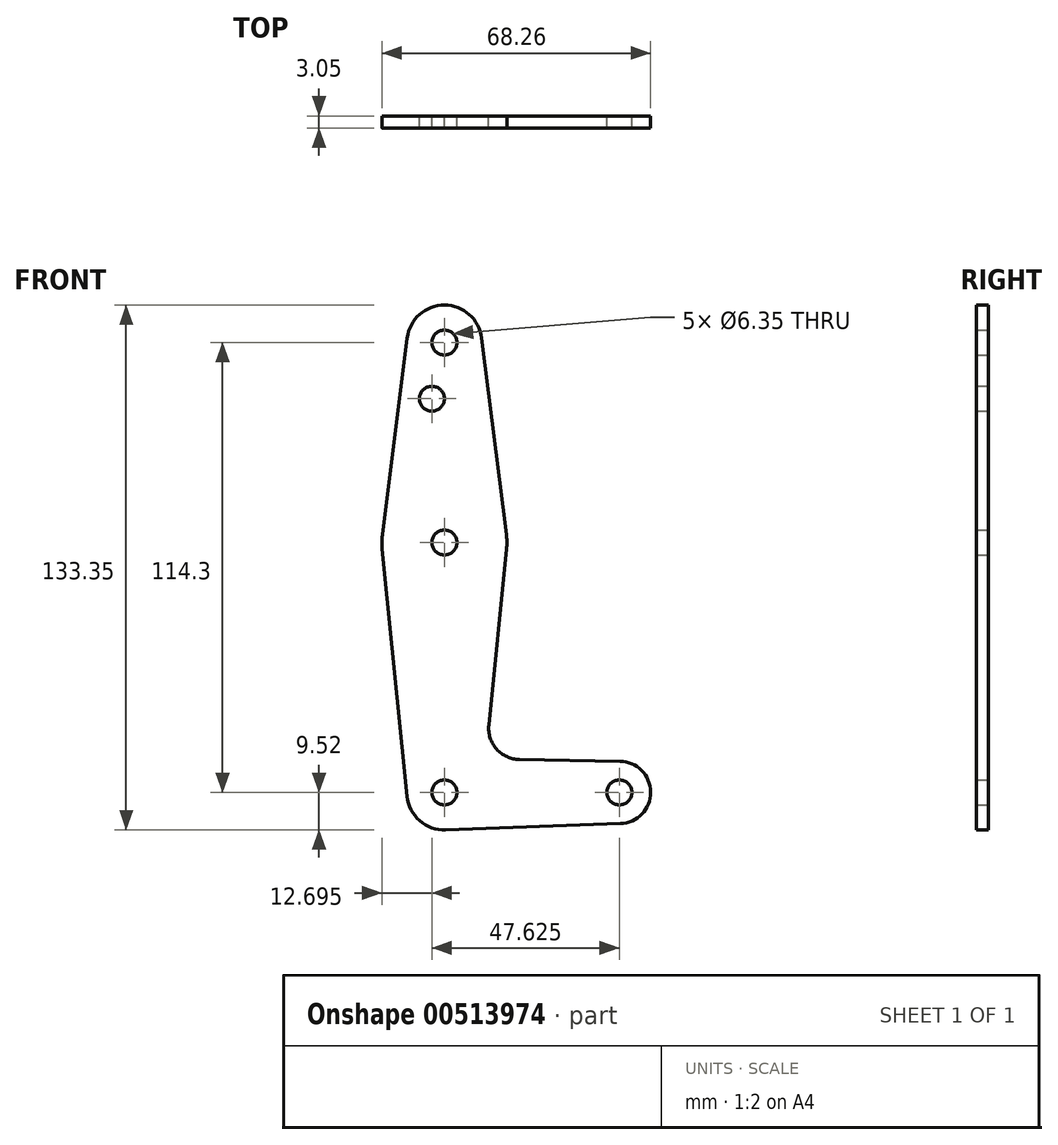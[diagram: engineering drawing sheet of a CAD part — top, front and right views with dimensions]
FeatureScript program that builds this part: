
annotation { "Feature Type Name" : "Feature", "Feature Type Description" : "" }
export const myFeature = defineFeature(function(context is Context, id is Id, definition is map)
    precondition{}
    {
        {
            var Q0;
            Q0=qCreatedBy(makeId("Front.planeOp"),FACE);
            var sketch = newSketch(context, id + "F0", { "sketchPlane" : qUnion([Q0])});
            skLineSegment(sketch, "E0", {"start": v(0, 114.3) * mm, "end": v(0, 0) * mm, "construction": true});
            skLineSegment(sketch, "E1", {"start": v(0, 0) * mm, "end": v(44.45, 0) * mm, "construction": true});
            skCircle(sketch, "E2", {"center": v(0, 114.3) * mm, "radius": 9.53 * mm});
            skCircle(sketch, "E3", {"center": v(0, 63.5) * mm, "radius": 15.88 * mm});
            skCircle(sketch, "E4", {"center": v(0, 0) * mm, "radius": 9.53 * mm});
            skCircle(sketch, "E5", {"center": v(44.45, 0) * mm, "radius": 7.94 * mm});
            skLineSegment(sketch, "E6", {"start": v(-9.45, 115.5) * mm, "end": v(-15.75, 65.48) * mm});
            skLineSegment(sketch, "E7", {"start": v(9.45, 115.5) * mm, "end": v(15.75, 65.48) * mm});
            skLineSegment(sketch, "E8", {"start": v(-15.8, 61.91) * mm, "end": v(-9.48, -0.95) * mm});
            skLineSegment(sketch, "E9", {"start": v(15.8, 61.91) * mm, "end": v(11.3, 17.1) * mm});
            skLineSegment(sketch, "E10", {"start": v(19.07, 8.36) * mm, "end": v(44.58, 7.94) * mm});
            skLineSegment(sketch, "E11", {"start": v(0.34, -9.52) * mm, "end": v(44.73, -7.93) * mm});
            skCircle(sketch, "E12", {"center": v(0, 114.3) * mm, "radius": 3.18 * mm});
            skCircle(sketch, "E13", {"center": v(0, 63.5) * mm, "radius": 3.18 * mm});
            skCircle(sketch, "E14", {"center": v(0, 0) * mm, "radius": 3.18 * mm});
            skCircle(sketch, "E15", {"center": v(44.45, 0) * mm, "radius": 3.18 * mm});
            skCircle(sketch, "E16", {"center": v(-3.18, 100.03) * mm, "radius": 3.18 * mm});
            skArc(sketch, "E17.filletArc", {"start": v(11.3, 17.1) * mm, "mid": v(13.26, 11.03) * mm, "end": v(19.07, 8.36) * mm});
            skSolve(sketch);
        }
        {
            var Q0;
            Q0 = qSketchRegion(id + "F0", true);
            extrude(context, id + "F1", {"entities" : qUnion([Q0]), "depth" : 3.05 * mm});
        }
    });
